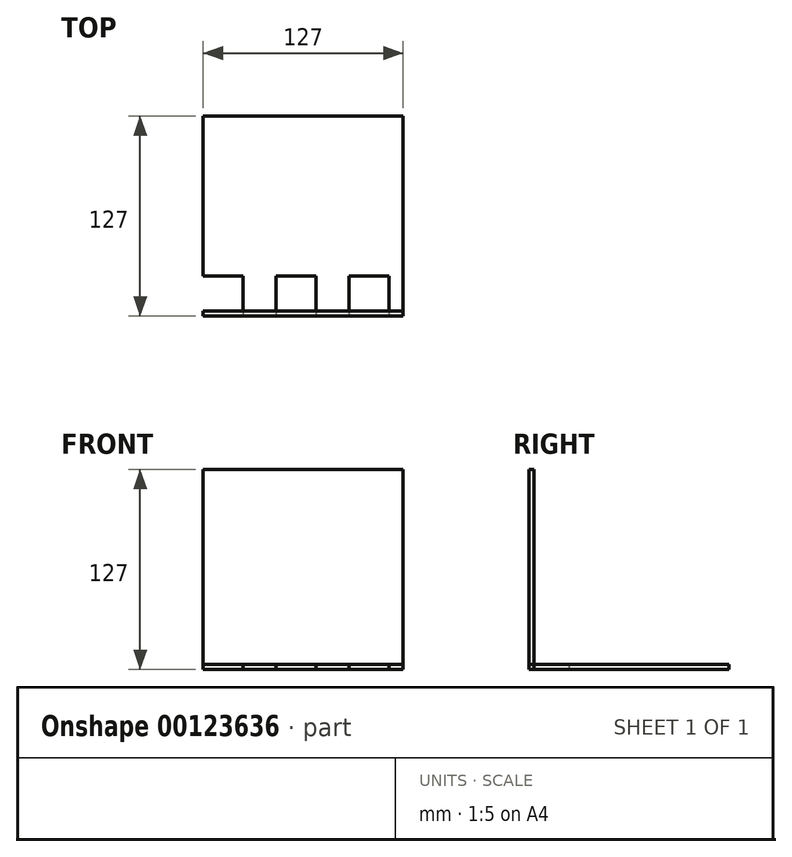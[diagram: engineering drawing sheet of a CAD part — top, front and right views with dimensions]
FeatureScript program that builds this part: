
annotation { "Feature Type Name" : "Feature", "Feature Type Description" : "" }
export const myFeature = defineFeature(function(context is Context, id is Id, definition is map)
    precondition{}
    {
        {
            var Q0;
            Q0=qCreatedBy(makeId("Top.planeOp"),FACE);
            var sketch = newSketch(context, id + "F0", { "sketchPlane" : qUnion([Q0])});
            skLineSegment(sketch, "E0.bottom", {"start": v(-63.5, 63.5) * mm, "end": v(63.5, 63.5) * mm});
            skLineSegment(sketch, "E0.top", {"start": v(-63.5, -63.5) * mm, "end": v(63.5, -63.5) * mm});
            skLineSegment(sketch, "E0.left", {"start": v(-63.5, 63.5) * mm, "end": v(-63.5, -63.5) * mm});
            skLineSegment(sketch, "E0.right", {"start": v(63.5, 63.5) * mm, "end": v(63.5, -63.5) * mm});
            skPoint(sketch, "E0.middle", {"position": v(0, 0) * mm});
            skSolve(sketch);
        }
        {
            var Q0;
            Q0 = qSketchRegion(id + "F0", true);
            extrude(context, id + "F1", {"entities" : qUnion([Q0]), "depth" : 3.17 * mm});
        }
        {
            var Q0;
            Q0=qCreatedBy(makeId("Top.planeOp"),FACE);
            var sketch = newSketch(context, id + "F2", { "sketchPlane" : qUnion([Q0])});
            skLineSegment(sketch, "E1.bottom", {"start": v(-63.5, -60.33) * mm, "end": v(63.5, -60.33) * mm});
            skLineSegment(sketch, "E1.top", {"start": v(-63.5, -63.5) * mm, "end": v(63.5, -63.5) * mm});
            skLineSegment(sketch, "E1.left", {"start": v(-63.5, -60.33) * mm, "end": v(-63.5, -63.5) * mm});
            skLineSegment(sketch, "E1.right", {"start": v(63.5, -60.33) * mm, "end": v(63.5, -63.5) * mm});
            skSolve(sketch);
        }
        {
            var Q0;
            Q0 = qSketchRegion(id + "F2", true);
            extrude(context, id + "F3", {"entities" : qUnion([Q0]), "depth" : 127 * mm});
        }
        {
            var Q0;
            Q0=makeQuery(id+"F1.opExtrude","SWEPT_FACE",FACE,{"disambiguationData":[OSD([sQuery(id+"F0.wireOp",EDGE,"E0.top")])]});
            var sketch = newSketch(context, id + "F4", { "sketchPlane" : qUnion([Q0])});
            skLineSegment(sketch, "E2.bottom", {"start": v(-63.56, 3.18) * mm, "end": v(-38.16, 3.18) * mm});
            skLineSegment(sketch, "E2.top", {"start": v(-63.56, 0) * mm, "end": v(-38.16, 0) * mm});
            skLineSegment(sketch, "E2.left", {"start": v(-63.56, 3.18) * mm, "end": v(-63.56, 0) * mm});
            skLineSegment(sketch, "E2.right", {"start": v(-38.16, 3.18) * mm, "end": v(-38.16, 0) * mm});
            skLineSegment(sketch, "E3.bottom", {"start": v(-17.2, 3.18) * mm, "end": v(8.2, 3.18) * mm});
            skLineSegment(sketch, "E3.top", {"start": v(-17.2, 0) * mm, "end": v(8.2, 0) * mm});
            skLineSegment(sketch, "E3.left", {"start": v(-17.2, 3.18) * mm, "end": v(-17.2, 0) * mm});
            skLineSegment(sketch, "E3.right", {"start": v(8.2, 3.18) * mm, "end": v(8.2, 0) * mm});
            skLineSegment(sketch, "E4.bottom", {"start": v(29.15, 3.18) * mm, "end": v(54.55, 3.18) * mm});
            skLineSegment(sketch, "E4.top", {"start": v(29.15, 0) * mm, "end": v(54.55, 0) * mm});
            skLineSegment(sketch, "E4.left", {"start": v(29.15, 3.18) * mm, "end": v(29.15, 0) * mm});
            skLineSegment(sketch, "E4.right", {"start": v(54.55, 3.18) * mm, "end": v(54.55, 0) * mm});
            skSolve(sketch);
        }
        {
            var Q0;
            {var subQ3=sQuery(id+"F4.wireOp",EDGE,"E2.right");Q0=makeQuery(id+"F4.imprint","IMPRINT",FACE,{"disambiguationData":[TD([[makeQuery(id+"F4.imprint","IMPRINT",EDGE,{"derivedFrom":subQ3}),-1.0]])]});}
            var Q1;
            Q1=makeQuery(id+"F4.imprint","IMPRINT",FACE,{"disambiguationData":[TD([[makeQuery(id+"F4.imprint","IMPRINT",EDGE,{"derivedFrom":sQuery(id+"F4.wireOp",EDGE,"E3.bottom")}),-1.0]])]});
            var Q2;
            Q2=makeQuery(id+"F4.imprint","IMPRINT",FACE,{"disambiguationData":[TD([[makeQuery(id+"F4.imprint","IMPRINT",EDGE,{"derivedFrom":sQuery(id+"F4.wireOp",EDGE,"E4.bottom")}),-1.0]])]});
            extrude(context, id + "F5", {"entities" : qUnion([Q0, Q1, Q2]), "operationType" : NewBodyOperationType.REMOVE, "oppositeDirection" : true, "depth" : 25.4 * mm});
        }
    });
